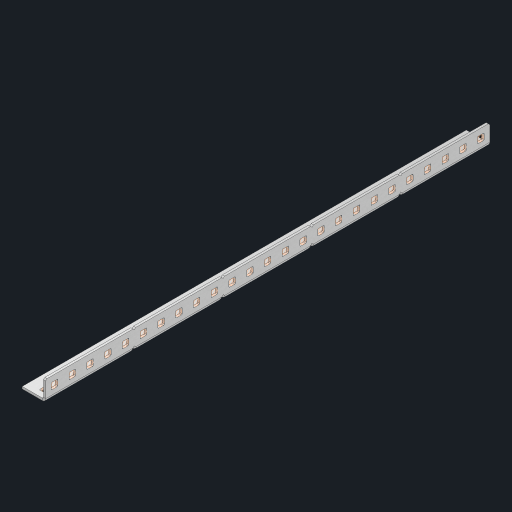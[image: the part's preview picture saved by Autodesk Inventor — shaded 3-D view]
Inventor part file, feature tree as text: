
AUTODESK INVENTOR PART (.ipt)
format: ipt  version: 2023 (Build 270158000, 158)  size: 856,576 bytes
history: native  units: in
note: dims shown in document units (in); Inventor stores cm internally (conversion verified against a paired STEP export)
features: other x55, extrude x49, sheet_metal_op x10, sketch x8, mirror x1, pattern_linear x1, chamfer x1
ambient origin geometry x8: Origin, YZ Plane, XZ Plane, XY Plane, X Axis, Y Axis, Z Axis, Center Point
bodies: Solid1 (feature_tree), Body (feature_tree)
feature tree (125):
  other  "Flange Pattern Plane"
  sheet_metal_op  "Flange Pattern"
  sheet_metal_op  "Body Pattern"
  other  "Arc Length"
  mirror  "Notch Mirror"
  pattern_linear  "Notch Pattern"  Spacing1=0.25in  [1 undecoded]
  chamfer  "End Chamfer"
  extrude  "Half Cut"  Depth=0.0625in
  sketch  "Sketch1"  dims[d0=1.5in]
  other  "Plate1"
  sketch  "Sketch2"  dims[d1=12.5in]
  other  "Plate2"
  sheet_metal_op  "Bend1"
  sheet_metal_op  "Corner1"
  sketch  "Sketch3"  dims[d2=0.0625in]
  other  "Flange Pattern Sketch"
  sketch  "Sketch7"  dims[d3=0.0625in]
  other  "Srf1"
  other  "Srf2"
  sketch  "Sketch8"  dims[d4=0.0312in]
  sketch  "Sketch9"  dims[d5=0.125in]
  other  "Srf91"
  sheet_metal_op  "Body Pattern Sketch"
  other  "Srf92"
  sketch  "Sketch13"  dims[d6=0.0625in]
  sketch  "Sketch14"  dims[d7=0.5in d8=90.0deg d9=0.0312in d10=0.25in d11=0.0625in d12=0.0625in d16=0.182in d17=0.02in d18=0.0625in d19=0.0in d20=0.25in d21=0.25in d46=0.172in d47=1.0in d48=0.0in d49=0.182in d50=0.02in d51=0.25in d52=0.25in d53=0.0625in d54=0.0in d55=0.172in d56=1.0in d57=0.0in d60=9.8425in d62=0.5in d63=0.3937in d65=0.5in d85=0.1473in d86=0.1782in d88=0.04in d89=0.0625in d90=0.0in d91=0.04in d92=0.0491in d95=2.5in d96=0.04in d97=0.25in d98=45.0deg d101=0.0in d102=2.497in d131=0.5in d132=9.8425in d134=0.5in d139=0.5in]
  other  "Srf856"
  other  "Srf1310"
  other  "Srf1311"
  other  "Srf1312"
  other  "Srf1376"
  other  "Srf1377"
  other  "Srf1728"
  other  "Srf1755"
  other  "Srf1878"
  other  "Srf1879"
  other  "Srf1880"
  other  "Srf1881"
  other  "Srf1882"
  other  "Srf1883"
  other  "Srf1884"
  other  "Srf1885"
  other  "Srf1886"
  other  "Srf1887"
  other  "Srf1888"
  other  "Srf1889"
  other  "Srf1890"
  other  "Srf1891"
  other  "Srf1892"
  other  "Srf1893"
  other  "Srf1894"
  other  "Srf1895"
  other  "Srf1896"
  other  "Srf1942"
  other  "Srf1943"
  other  "Srf1944"
  other  "Srf1945"
  other  "Srf1946"
  other  "Srf1947"
  other  "Srf1948"
  other  "Srf1949"
  other  "Srf1950"
  other  "Srf1951"
  other  "Srf1952"
  other  "Srf1953"
  other  "Srf1954"
  other  "Srf1955"
  other  "Srf1956"
  other  "Srf1957"
  other  "Srf1958"
  other  "Srf1959"
  other  "Srf1960"
  sheet_metal_op  "Flange Stamp"
  sheet_metal_op  "Flange Circle"
  sheet_metal_op  "Body Stamp"
  sheet_metal_op  "Body Circle"
  sheet_metal_op  "Notch"
  extrude  "ExtrusionSrf2"  Depth=0.0625in
  extrude  "ExtrusionSrf92"  Depth=0.5in
  extrude  "ExtrusionSrf856"  Depth=0.02in
  extrude  "ExtrusionSrf1310"  Depth=0.0625in
  extrude  "ExtrusionSrf1311"  TaperAngle=0.0deg  [1 undecoded]
  extrude  "ExtrusionSrf1312"  Depth=0.5in
  extrude  "ExtrusionSrf1376"  Depth=0.5in
  extrude  "ExtrusionSrf1377"  Depth=0.5in
  extrude  "ExtrusionSrf1728"  Depth=0.5in TaperAngle=0.0deg
  extrude  "ExtrusionSrf1755"  Depth=0.5in
  extrude  "ExtrusionSrf1878"  Depth=0.02in
  extrude  "ExtrusionSrf1879"  Depth=0.5in
  extrude  "ExtrusionSrf1880"  Depth=0.5in
  extrude  "ExtrusionSrf1881"  Depth=0.0625in
  extrude  "ExtrusionSrf1882"  TaperAngle=0.0deg  [1 undecoded]
  extrude  "ExtrusionSrf1883"  Depth=0.5in
  extrude  "ExtrusionSrf1884"  Depth=0.5in TaperAngle=0.0deg
  extrude  "ExtrusionSrf1885"  Depth=0.5in
  extrude  "ExtrusionSrf1886"  Depth=0.5in
  extrude  "ExtrusionSrf1887"  Depth=0.5in
  extrude  "ExtrusionSrf1888"  Depth=0.5in
  extrude  "ExtrusionSrf1889"  Depth=0.5in
  extrude  "ExtrusionSrf1890"  Depth=0.0625in
  extrude  "ExtrusionSrf1891"  TaperAngle=0.0deg  [1 undecoded]
  extrude  "ExtrusionSrf1892"  Depth=0.5in
  extrude  "ExtrusionSrf1893"  Depth=0.5in
  extrude  "ExtrusionSrf1894"  Depth=0.5in
  extrude  "ExtrusionSrf1895"  Depth=0.5in TaperAngle=45.0deg
  extrude  "ExtrusionSrf1896"  TaperAngle=0.0deg  [1 undecoded]
  extrude  "ExtrusionSrf1942"  Depth=0.5in
  extrude  "ExtrusionSrf1943"  Depth=0.5in
  extrude  "ExtrusionSrf1944"  Depth=0.5in
  extrude  "ExtrusionSrf1945"  Depth=0.5in
  extrude  "ExtrusionSrf1946"  Depth=0.5in
  extrude  "ExtrusionSrf1947"  [1 undecoded]
  extrude  "ExtrusionSrf1948"  [1 undecoded]
  extrude  "ExtrusionSrf1949"  [1 undecoded]
  extrude  "ExtrusionSrf1950"  [1 undecoded]
  extrude  "ExtrusionSrf1951"  [1 undecoded]
  extrude  "ExtrusionSrf1952"  [1 undecoded]
  extrude  "ExtrusionSrf1953"  [1 undecoded]
  extrude  "ExtrusionSrf1954"  [1 undecoded]
  extrude  "ExtrusionSrf1955"  [1 undecoded]
  extrude  "ExtrusionSrf1956"  [1 undecoded]
  extrude  "ExtrusionSrf1957"  [1 undecoded]
  extrude  "ExtrusionSrf1958"  [1 undecoded]
  extrude  "ExtrusionSrf1959"  [1 undecoded]
  extrude  "ExtrusionSrf1960"  [1 undecoded]
note: 19 required parameter values undecoded (feature->parameter linkage not recoverable at this tier; creation-order binding heuristic only, values carry confidence <= 0.55)
